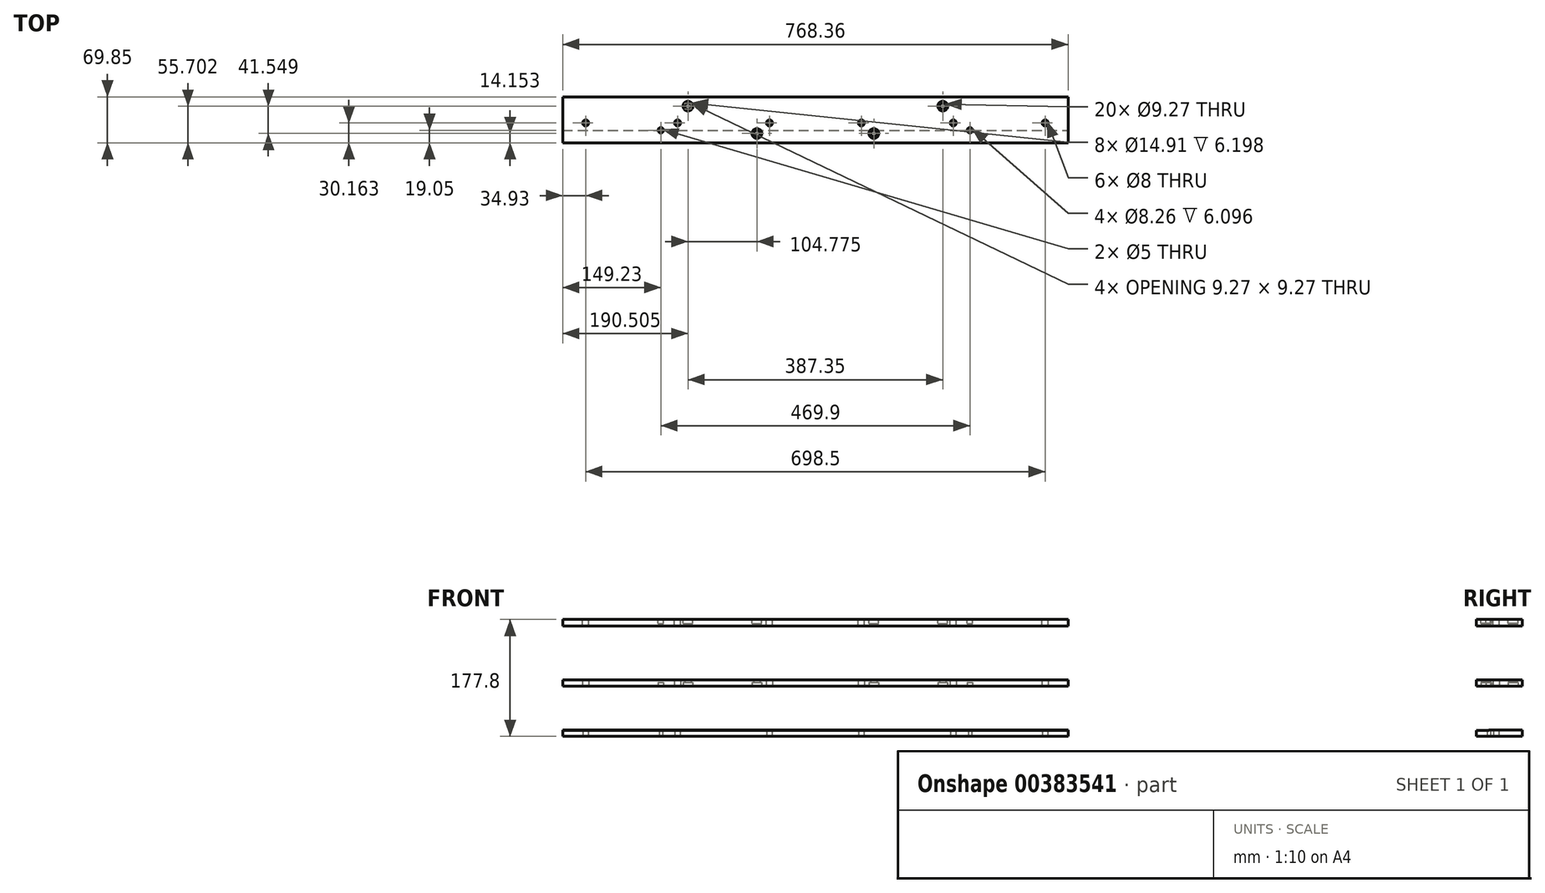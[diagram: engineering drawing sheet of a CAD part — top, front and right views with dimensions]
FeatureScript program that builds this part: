
annotation { "Feature Type Name" : "Feature", "Feature Type Description" : "" }
export const myFeature = defineFeature(function(context is Context, id is Id, definition is map)
    precondition{}
    {
        {
            var Q0;
            Q0=qCreatedBy(makeId("Top.planeOp"),FACE);
            var sketch = newSketch(context, id + "F0", { "sketchPlane" : qUnion([Q0])});
            skLineSegment(sketch, "E0.bottom", {"start": v(-384.18, 25.4) * mm, "end": v(384.18, 25.4) * mm});
            skLineSegment(sketch, "E0.top", {"start": v(-384.18, -44.45) * mm, "end": v(384.18, -44.45) * mm});
            skLineSegment(sketch, "E0.left", {"start": v(-384.18, 25.4) * mm, "end": v(-384.18, -44.45) * mm});
            skLineSegment(sketch, "E0.right", {"start": v(384.18, 25.4) * mm, "end": v(384.18, -44.45) * mm});
            skCircle(sketch, "E1", {"center": v(234.95, -25.4) * mm, "radius": 2.5 * mm});
            skCircle(sketch, "E2", {"center": v(349.25, -14.29) * mm, "radius": 4 * mm});
            skCircle(sketch, "E3", {"center": v(209.55, -14.29) * mm, "radius": 4 * mm});
            skCircle(sketch, "E4", {"center": v(69.85, -14.29) * mm, "radius": 4 * mm});
            skCircle(sketch, "E5", {"center": v(-349.25, -14.29) * mm, "radius": 4 * mm});
            skCircle(sketch, "E6", {"center": v(-209.55, -14.29) * mm, "radius": 4 * mm});
            skCircle(sketch, "E7", {"center": v(-69.85, -14.29) * mm, "radius": 4 * mm});
            skCircle(sketch, "E8", {"center": v(-234.95, -25.4) * mm, "radius": 2.5 * mm});
            skSolve(sketch);
        }
        {
            var Q0;
            Q0 = qSketchRegion(id + "F0", true);
            extrude(context, id + "F1", {"entities" : qUnion([Q0]), "depth" : 9.9 * mm});
        }
        {
            var Q0;
            Q0=makeQuery(id+"F1.opExtrude","CAP_FACE",FACE,{"disambiguationData":[OSD([sQuery(id+"F0.wireOp",EDGE,"E0.bottom"),sQuery(id+"F0.wireOp",EDGE,"E0.top"),sQuery(id+"F0.wireOp",EDGE,"E0.left"),sQuery(id+"F0.wireOp",EDGE,"E0.right"),sQuery(id+"F0.wireOp",EDGE,"E1"),sQuery(id+"F0.wireOp",EDGE,"E2"),sQuery(id+"F0.wireOp",EDGE,"E3"),sQuery(id+"F0.wireOp",EDGE,"E4"),sQuery(id+"F0.wireOp",EDGE,"E5"),sQuery(id+"F0.wireOp",EDGE,"E6"),sQuery(id+"F0.wireOp",EDGE,"E7")])],"isStart":false});
            var sketch = newSketch(context, id + "F2", { "sketchPlane" : qUnion([Q0])});
            skLineSegment(sketch, "E9.bottom", {"start": v(-384.18, -44.45) * mm, "end": v(384.18, -44.45) * mm});
            skLineSegment(sketch, "E9.top", {"start": v(-384.18, -25.4) * mm, "end": v(384.18, -25.4) * mm});
            skLineSegment(sketch, "E9.left", {"start": v(-384.18, -44.45) * mm, "end": v(-384.18, -25.4) * mm});
            skLineSegment(sketch, "E9.right", {"start": v(384.18, -44.45) * mm, "end": v(384.18, -25.4) * mm});
            skSolve(sketch);
        }
        {
            var Q0;
            Q0 = qSketchRegion(id + "F2", true);
            extrude(context, id + "F3", {"entities" : qUnion([Q0]), "operationType" : NewBodyOperationType.REMOVE, "oppositeDirection" : true, "depth" : 0.5 * mm});
        }
        {
            var Q0;
            Q0=qCreatedBy(makeId("Top.planeOp"),FACE);
            cPlane(context, id + "F4", {"entities" : qUnion([Q0]), "cplaneType" : CPlaneType.OFFSET, "offset" : 76.2 * mm, "width" : 152.4 * mm, "height" : 152.4 * mm});
        }
        {
            var Q0;
            Q0=qCreatedBy(id+"F4.planeOp",FACE);
            var sketch = newSketch(context, id + "F5", { "sketchPlane" : qUnion([Q0])});
            skLineSegment(sketch, "E10.bottom", {"start": v(-384.18, 25.4) * mm, "end": v(384.18, 25.4) * mm});
            skLineSegment(sketch, "E10.top", {"start": v(-384.18, -44.45) * mm, "end": v(384.18, -44.45) * mm});
            skLineSegment(sketch, "E10.left", {"start": v(-384.18, 25.4) * mm, "end": v(-384.18, -44.45) * mm});
            skLineSegment(sketch, "E10.right", {"start": v(384.18, 25.4) * mm, "end": v(384.18, -44.45) * mm});
            skCircle(sketch, "E11", {"center": v(-349.25, -14.29) * mm, "radius": 4.64 * mm});
            skCircle(sketch, "E12", {"center": v(-209.55, -14.29) * mm, "radius": 4.64 * mm});
            skCircle(sketch, "E13", {"center": v(-69.85, -14.29) * mm, "radius": 4.64 * mm});
            skCircle(sketch, "E14", {"center": v(69.85, -14.29) * mm, "radius": 4.64 * mm});
            skCircle(sketch, "E15", {"center": v(209.55, -14.29) * mm, "radius": 4.64 * mm});
            skCircle(sketch, "E16", {"center": v(349.25, -14.29) * mm, "radius": 4.64 * mm});
            skCircle(sketch, "E17", {"center": v(-193.68, 11.25) * mm, "radius": 4.64 * mm});
            skCircle(sketch, "E18", {"center": v(-88.9, -30.3) * mm, "radius": 4.64 * mm});
            skCircle(sketch, "E19.MirrorC", {"center": v(88.9, -30.3) * mm, "radius": 4.64 * mm});
            skCircle(sketch, "E20.MirrorC", {"center": v(193.68, 11.25) * mm, "radius": 4.64 * mm});
            skSolve(sketch);
        }
        {
            var Q0;
            Q0 = qSketchRegion(id + "F5", true);
            extrude(context, id + "F6", {"entities" : qUnion([Q0]), "depth" : 9.9 * mm});
        }
        {
            var Q0;
            Q0=makeQuery(id+"F6.opExtrude","CAP_FACE",FACE,{"disambiguationData":[OSD([sQuery(id+"F5.wireOp",EDGE,"E10.bottom"),sQuery(id+"F5.wireOp",EDGE,"E10.top"),sQuery(id+"F5.wireOp",EDGE,"E10.left"),sQuery(id+"F5.wireOp",EDGE,"E10.right"),sQuery(id+"F5.wireOp",EDGE,"E11"),sQuery(id+"F5.wireOp",EDGE,"E12"),sQuery(id+"F5.wireOp",EDGE,"E13"),sQuery(id+"F5.wireOp",EDGE,"E14"),sQuery(id+"F5.wireOp",EDGE,"E15"),sQuery(id+"F5.wireOp",EDGE,"E16"),sQuery(id+"F5.wireOp",EDGE,"E17"),sQuery(id+"F5.wireOp",EDGE,"E18"),sQuery(id+"F5.wireOp",EDGE,"f23d43c9-97b8-401b-9fae-ae484db2d59a"),sQuery(id+"F5.wireOp",EDGE,"c121301e-1d55-481c-90d3-8e597230d4d40.MirrorC")])],"isStart":true});
            var sketch = newSketch(context, id + "F7", { "sketchPlane" : qUnion([Q0])});
            skCircle(sketch, "E21", {"center": v(-234.95, 25.4) * mm, "radius": 4.13 * mm});
            skCircle(sketch, "E22", {"center": v(234.95, 25.4) * mm, "radius": 4.13 * mm});
            skSolve(sketch);
        }
        {
            var Q0;
            Q0 = qSketchRegion(id + "F7", true);
            extrude(context, id + "F8", {"entities" : qUnion([Q0]), "operationType" : NewBodyOperationType.REMOVE, "oppositeDirection" : true, "depth" : 6.1 * mm});
        }
        {
            var Q0;
            Q0=qCreatedBy(makeId("Front.planeOp"),FACE);
            cPlane(context, id + "F9", {"entities" : qUnion([Q0]), "cplaneType" : CPlaneType.OFFSET, "offset" : 25.4 * mm, "width" : 152.4 * mm, "height" : 152.4 * mm});
        }
        {
            var Q0;
            Q0=makeQuery(id+"F6.opExtrude","CAP_FACE",FACE,{"disambiguationData":[OSD([sQuery(id+"F5.wireOp",EDGE,"E10.bottom"),sQuery(id+"F5.wireOp",EDGE,"E10.top"),sQuery(id+"F5.wireOp",EDGE,"E10.left"),sQuery(id+"F5.wireOp",EDGE,"E10.right"),sQuery(id+"F5.wireOp",EDGE,"E11"),sQuery(id+"F5.wireOp",EDGE,"E12"),sQuery(id+"F5.wireOp",EDGE,"E13"),sQuery(id+"F5.wireOp",EDGE,"E14"),sQuery(id+"F5.wireOp",EDGE,"E15"),sQuery(id+"F5.wireOp",EDGE,"E16"),sQuery(id+"F5.wireOp",EDGE,"E17"),sQuery(id+"F5.wireOp",EDGE,"E18"),sQuery(id+"F5.wireOp",EDGE,"f23d43c9-97b8-401b-9fae-ae484db2d59a"),sQuery(id+"F5.wireOp",EDGE,"c121301e-1d55-481c-90d3-8e597230d4d40.MirrorC")])],"isStart":true});
            var sketch = newSketch(context, id + "F10", { "sketchPlane" : qUnion([Q0])});
            skCircle(sketch, "E23", {"center": v(-193.68, -11.25) * mm, "radius": 7.45 * mm});
            skCircle(sketch, "E24", {"center": v(-88.9, 30.3) * mm, "radius": 7.45 * mm});
            skCircle(sketch, "E25", {"center": v(88.9, 30.3) * mm, "radius": 7.45 * mm});
            skCircle(sketch, "E26", {"center": v(193.68, -11.25) * mm, "radius": 7.45 * mm});
            skSolve(sketch);
        }
        {
            var Q0;
            Q0 = qSketchRegion(id + "F10", true);
            extrude(context, id + "F11", {"entities" : qUnion([Q0]), "operationType" : NewBodyOperationType.REMOVE, "oppositeDirection" : true, "depth" : 6.2 * mm});
        }
        {
            var Q0;
            Q0=qCreatedBy(makeId("Top.planeOp"),FACE);
            cPlane(context, id + "F12", {"entities" : qUnion([Q0]), "cplaneType" : CPlaneType.OFFSET, "offset" : 127 * mm, "width" : 152.4 * mm, "height" : 152.4 * mm});
        }
        {
            var Q0;
            Q0=makeQuery(id+"F6.opExtrude","SWEPT_BODY",BODY,{"disambiguationData":[OSD([sQuery(id+"F5.wireOp",EDGE,"E10.bottom"),sQuery(id+"F5.wireOp",EDGE,"E10.top"),sQuery(id+"F5.wireOp",EDGE,"E10.left"),sQuery(id+"F5.wireOp",EDGE,"E10.right"),sQuery(id+"F5.wireOp",EDGE,"E11"),sQuery(id+"F5.wireOp",EDGE,"E12"),sQuery(id+"F5.wireOp",EDGE,"E13"),sQuery(id+"F5.wireOp",EDGE,"E14"),sQuery(id+"F5.wireOp",EDGE,"E15"),sQuery(id+"F5.wireOp",EDGE,"E16"),sQuery(id+"F5.wireOp",EDGE,"E17"),sQuery(id+"F5.wireOp",EDGE,"E18"),sQuery(id+"F5.wireOp",EDGE,"E19.MirrorC"),sQuery(id+"F5.wireOp",EDGE,"E20.MirrorC")])]});
            var Q1;
            Q1=qCreatedBy(id+"F12.planeOp",FACE);
            mirror(context, id + "F13", {"entities" : qUnion([Q0]), "mirrorPlane" : qUnion([Q1])});
        }
    });
